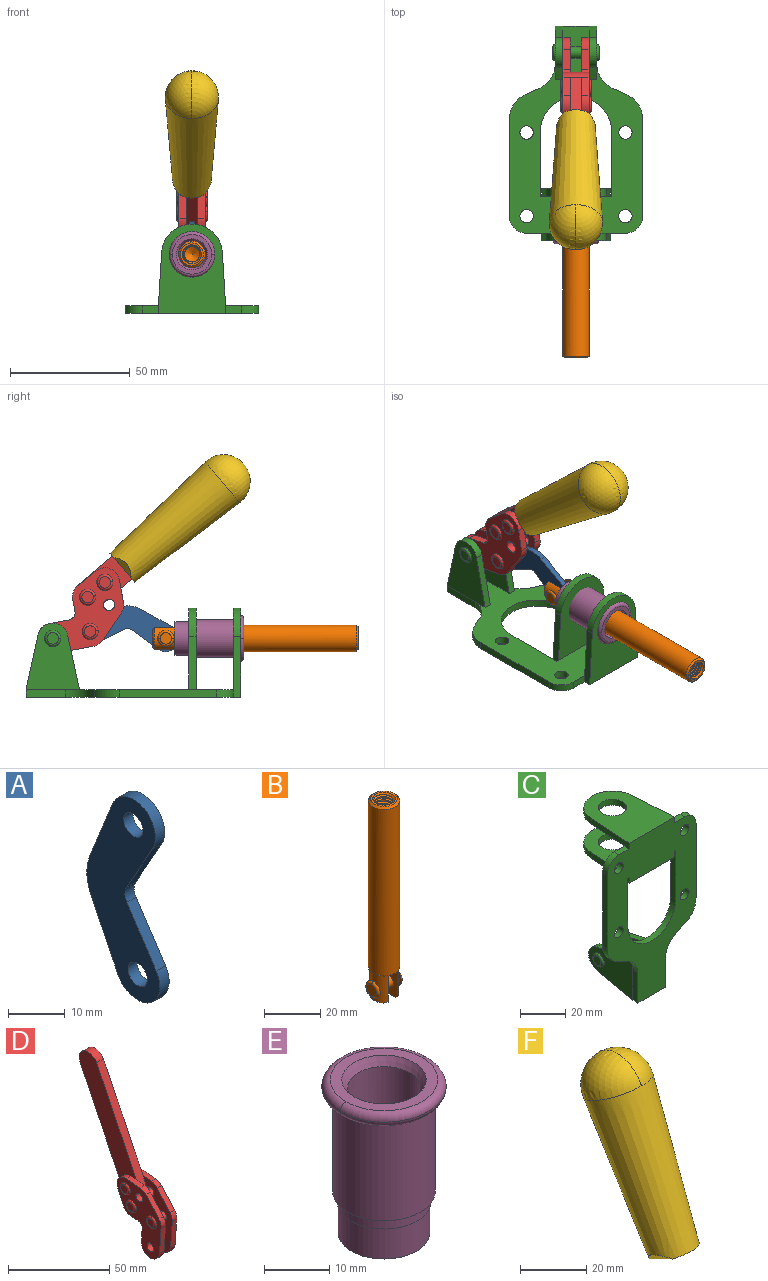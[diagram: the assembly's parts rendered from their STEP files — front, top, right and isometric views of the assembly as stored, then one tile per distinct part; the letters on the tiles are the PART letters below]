
ASSEMBLY  parts=6 mates=6
PART A: 12 faces, bbox 2.3x18.2x42.8 mm
  f0: cylinder r=2.4mm len=4.8mm, axis (1,0,0), area 34.9mm2, adj f4,f11
  f1: cylinder r=10.41mm len=8.47mm, axis (1,0,0), area 20.2mm2, adj f4,f9,f10,f11
  f2: cylinder r=3.05mm len=3.16mm, axis (1,0,0), area 7.7mm2, adj f4,f6,f7,f11
  f3: cylinder r=2.4mm len=4.8mm, axis (1,0,0), area 34.9mm2, adj f4,f11
  f4: plane 42.81x18.23mm, normal (-1,0,0), area 414.1mm2, adj f0,f1,f2,f3,f5,f6,f7,f8
  f5: cylinder r=5.54mm len=10.67mm, axis (1,0,0), area 41.8mm2, adj f4,f6,f10,f11
  f6: plane 11.66x6.53mm, normal (0,-0.87,-0.49), area 30.9mm2, adj f2,f4,f5,f11
  f7: plane 11.17x7.33mm, normal (0,-0.84,0.55), area 30.9mm2, adj f2,f4,f8,f11
  f8: cylinder r=5.54mm len=10.51mm, axis (1,0,0), area 41.8mm2, adj f4,f7,f9,f11
  f9: plane 13.67x6.67mm, normal (0,0.9,-0.44), area 35.1mm2, adj f1,f4,f8,f11
  f10: plane 14.1x5.7mm, normal (0,0.93,0.37), area 35.1mm2, adj f1,f4,f5,f11
  f11: plane 42.81x18.23mm, normal (1,0,0), area 414.1mm2, adj f0,f1,f2,f3,f5,f6,f7,f8
PART B: 48 faces, bbox 12.6x11.1x86.1 mm
  f0: torus R=2.41mm, axis (-1,0,0), area 15mm2, adj f30,f32,f34
  f1: torus R=2.41mm, axis (-1,0,0), area 15mm2, adj f29,f31,f33
  f2: cylinder r=5.54mm len=72.39mm, axis (0,0,1), area 2518.5mm2, adj f3,f4,f42,f43
  f3: cone r=5.54mm half-angle=45deg, axis (0,0,1), area 7.6mm2, adj f2,f5,f41
  f4: cone r=5.54mm half-angle=45deg, axis (0,0,-1), area 34.9mm2, adj f2,f39
  f5: cylinder r=5.08mm len=11.48mm, axis (0,0,1), area 108.3mm2, adj f3,f7,f8,f41
  f6: cylinder r=2.41mm len=4.83mm, axis (-1,0,0), area 71.2mm2, adj f40,f41
  f7: cylinder r=2.41mm len=4.83mm, axis (-1,0,0), area 7.6mm2, adj f5,f34
  f8: cone r=5.08mm half-angle=45deg, axis (0,0,1), area 10.6mm2, adj f5,f37,f41
  f9: cone r=3.98mm half-angle=45deg, axis (0,0,1), area 17.6mm2, adj f27,f39,f45,f46,f47
  f10: cylinder r=2.41mm len=4.83mm, axis (-1,0,0), area 7.6mm2, adj f33,f38
  f11: cylinder r=3.2mm len=6.4mm, axis (0,0,1), area 78.4mm2, adj f12,f28,f44,f45,f47
  f12: cylinder r=3.2mm len=6.4mm, axis (0,0,1), area 10.5mm2, adj f11,f13,f45,f47
  f13: cylinder r=3.2mm len=6.4mm, axis (0,0,1), area 10.5mm2, adj f12,f14,f45,f47
  f14: cylinder r=3.2mm len=6.4mm, axis (0,0,1), area 10.5mm2, adj f13,f15,f45,f47
  f15: cylinder r=3.2mm len=6.4mm, axis (0,0,1), area 10.5mm2, adj f14,f16,f45,f47
  f16: cylinder r=3.2mm len=6.4mm, axis (0,0,1), area 10.5mm2, adj f15,f17,f45,f47
  f17: cylinder r=3.2mm len=6.4mm, axis (0,0,1), area 10.5mm2, adj f16,f18,f45,f47
  f18: cylinder r=3.2mm len=6.4mm, axis (0,0,1), area 10.5mm2, adj f17,f19,f45,f47
  f19: cylinder r=3.2mm len=6.4mm, axis (0,0,1), area 10.5mm2, adj f18,f20,f45,f47
  f20: cylinder r=3.2mm len=6.4mm, axis (0,0,1), area 10.5mm2, adj f19,f21,f45,f47
  f21: cylinder r=3.2mm len=6.4mm, axis (0,0,1), area 10.5mm2, adj f20,f22,f45,f47
  f22: cylinder r=3.2mm len=6.4mm, axis (0,0,1), area 10.5mm2, adj f21,f23,f45,f47
  f23: cylinder r=3.2mm len=6.4mm, axis (0,0,1), area 10.5mm2, adj f22,f24,f45,f47
  f24: cylinder r=3.2mm len=6.4mm, axis (0,0,1), area 10.5mm2, adj f23,f25,f45,f47
  f25: cylinder r=3.2mm len=6.4mm, axis (0,0,1), area 10.5mm2, adj f24,f26,f45,f47
  f26: cylinder r=3.2mm len=6.4mm, axis (0,0,1), area 10.5mm2, adj f25,f27,f45,f47
  f27: cylinder r=3.2mm len=6.4mm, axis (0,0,1), area 7.4mm2, adj f9,f26,f45,f47
  f28: cone r=3.2mm half-angle=60deg, axis (0,0,1), area 37.2mm2, adj f11
  f29: plane 4.83x4.83mm, normal (-1,0,0), area 18.3mm2, adj f1,f31
  f30: plane 4.83x4.83mm, normal (1,0,0), area 18.3mm2, adj f0,f32
  f31: torus R=2.41mm, axis (-1,0,0), area 15mm2, adj f1,f29,f33
  f32: torus R=2.41mm, axis (-1,0,0), area 15mm2, adj f0,f30,f34
  f33: plane 6.83x6.83mm, normal (1,0,0), area 18.3mm2, adj f1,f10,f31
  f34: plane 6.83x6.83mm, normal (-1,0,0), area 18.3mm2, adj f0,f7,f32
  f35: cone r=5.08mm half-angle=45deg, axis (0,0,1), area 10.6mm2, adj f36,f38,f40
  f36: plane 7.25x1.97mm, normal (0,0,-1), area 10mm2, adj f35,f40
  f37: plane 7.25x1.97mm, normal (0,0,-1), area 10mm2, adj f8,f41
  f38: cylinder r=5.08mm len=11.48mm, axis (0,0,1), area 108.3mm2, adj f10,f35,f40,f42
  f39: plane 9.55x9.55mm, normal (0,0,1), area 22mm2, adj f4,f9
  f40: plane 12.76x10.09mm, normal (1,0,0), area 95.7mm2, adj f6,f35,f36,f38,f42,f43
  f41: plane 12.76x10.09mm, normal (-1,0,0), area 95.7mm2, adj f3,f5,f6,f8,f37,f43
  f42: cone r=5.54mm half-angle=45deg, axis (0,0,1), area 7.6mm2, adj f2,f38,f40
  f43: plane 11.07x4.7mm, normal (0,0,-1), area 50.4mm2, adj f2,f40,f41
  f44: plane 0.89x0.62mm, normal (-1,0,0), area 0.3mm2, adj f11,f45,f46,f47
  f45: bspline ~24.8x7.63mm, area 266.6mm2, adj f9,f11,f12,f13,f14,f15,f16,f17
  f46: bspline ~24.87x7.63mm, area 73.6mm2, adj f9,f44,f45,f47
  f47: bspline ~24.98x7.63mm, area 272.5mm2, adj f9,f11,f12,f13,f14,f15,f16,f17
PART C: 55 faces, bbox 55.7x37.4x89.8 mm
  f0: torus R=2.41mm, axis (-1,0,0), area 15mm2, adj f11,f15,f25
  f1: torus R=2.41mm, axis (-1,0,0), area 15mm2, adj f10,f12,f22
  f2: cylinder r=2.78mm len=5.56mm, axis (0,-1,0), area 54.2mm2, adj f30,f54
  f3: cylinder r=14.99mm len=29.97mm, axis (0,-1,0), area 145.9mm2, adj f30,f49,f53,f54
  f4: cylinder r=2.78mm len=5.56mm, axis (0,-1,0), area 54.2mm2, adj f30,f54
  f5: cylinder r=2.78mm len=5.56mm, axis (0,-1,0), area 54.2mm2, adj f30,f54
  f6: cylinder r=2.78mm len=5.56mm, axis (0,-1,0), area 54.2mm2, adj f30,f54
  f7: cylinder r=6.35mm len=12.7mm, axis (0,0,1), area 123.6mm2, adj f27,f51
  f8: cylinder r=6.35mm len=12.7mm, axis (0,0,-1), area 124.7mm2, adj f21,f35
  f9: cylinder r=2.41mm len=11.18mm, axis (-1,0,0), area 169.4mm2, adj f16,f19
  f10: plane 4.83x4.83mm, normal (1,0,0), area 18.3mm2, adj f1,f12
  f11: plane 4.83x4.83mm, normal (-1,0,0), area 18.3mm2, adj f0,f15
  f12: torus R=2.41mm, axis (-1,0,0), area 15mm2, adj f1,f10,f22
  f13: cylinder r=6.35mm len=12.41mm, axis (1,0,0), area 53.4mm2, adj f18,f19,f22,f23
  f14: cylinder r=6.35mm len=12.41mm, axis (-1,0,0), area 53.4mm2, adj f16,f17,f24,f25
  f15: torus R=2.41mm, axis (-1,0,0), area 15mm2, adj f0,f11,f25
  f16: plane 27.86x22.35mm, normal (1,0,0), area 425.4mm2, adj f9,f14,f17,f24,f30
  f17: plane 22.86x4.97mm, normal (0,0.21,0.98), area 72.5mm2, adj f14,f16,f25,f30
  f18: plane 22.86x4.97mm, normal (0,0.21,0.98), area 72.5mm2, adj f13,f19,f22,f30
  f19: plane 27.86x22.35mm, normal (-1,0,0), area 425.4mm2, adj f9,f13,f18,f23,f30
  f20: cylinder r=12.7mm len=25.35mm, axis (0,0,-1), area 119.8mm2, adj f21,f34,f35,f36
  f21: plane 34.21x28.07mm, normal (0,0,-1), area 702.4mm2, adj f8,f20,f30,f34,f36
  f22: plane 27.96x22.45mm, normal (1,0,0), area 407.2mm2, adj f1,f12,f13,f18,f23,f30,f42,f43
  f23: plane 22.86x4.97mm, normal (0,0.21,-0.98), area 72.5mm2, adj f13,f19,f22,f44
  f24: plane 22.86x4.97mm, normal (0,0.21,-0.98), area 72.5mm2, adj f14,f16,f25,f44
  f25: plane 27.86x22.35mm, normal (-1,0,0), area 407.1mm2, adj f0,f14,f15,f17,f24,f30,f45,f46
  f26: plane 3.1x0.95mm, normal (0,0,-1), area 2.7mm2, adj f30,f49,f50,f54
  f27: plane 34.21x28.07mm, normal (0,0,1), area 702.4mm2, adj f7,f28,f30,f50,f52
  f28: cylinder r=12.7mm len=25.35mm, axis (0,0,1), area 118.8mm2, adj f27,f50,f51,f52
  f29: plane 3.1x0.95mm, normal (0,0,-1), area 2.7mm2, adj f30,f52,f53,f54
  f30: plane 86.54x55.63mm, normal (0,1,0), area 2362.9mm2, adj f2,f3,f4,f5,f6,f16,f17,f18
  f31: plane 40.56x3.1mm, normal (-1,0,0), area 125.7mm2, adj f30,f32,f48,f54
  f32: cylinder r=7.11mm len=7.11mm, axis (0,-1,0), area 34.6mm2, adj f30,f31,f33,f54
  f33: plane 6.67x3.1mm, normal (0,0,1), area 20.4mm2, adj f30,f32,f34,f54
  f34: plane 25.39x3.13mm, normal (-1,0.06,0), area 79.5mm2, adj f20,f21,f33,f35,f54
  f35: plane 37.31x28.45mm, normal (0,0,1), area 789.9mm2, adj f8,f20,f34,f36,f54
  f36: plane 25.39x3.13mm, normal (1,0.06,0), area 79.5mm2, adj f20,f21,f35,f37,f54
  f37: plane 6.67x3.1mm, normal (0,0,1), area 20.4mm2, adj f30,f36,f38,f54
  f38: cylinder r=7.11mm len=7.11mm, axis (0,-1,0), area 34.6mm2, adj f30,f37,f39,f54
  f39: plane 40.56x3.1mm, normal (1,0,0), area 125.7mm2, adj f30,f38,f40,f54
  f40: cylinder r=11.18mm len=10.16mm, axis (0,-1,0), area 39.5mm2, adj f30,f39,f41,f54
  f41: plane 6.09x3.1mm, normal (0.42,0,-0.91), area 20.8mm2, adj f30,f40,f42,f54
  f42: cylinder r=11.18mm len=9.41mm, axis (0,-1,0), area 37.2mm2, adj f22,f30,f41,f43,f54
  f43: plane 16.5x3.1mm, normal (1,0,0), area 51.1mm2, adj f22,f42,f44,f54
  f44: plane 17.37x3.1mm, normal (0,0,-1), area 53.8mm2, adj f23,f24,f30,f43,f45,f54
  f45: plane 16.5x3.1mm, normal (-1,0,0), area 51.1mm2, adj f25,f44,f46,f54
  f46: cylinder r=11.18mm len=9.41mm, axis (0,-1,0), area 37.2mm2, adj f25,f30,f45,f47,f54
  f47: plane 6.09x3.1mm, normal (-0.42,0,-0.91), area 20.8mm2, adj f30,f46,f48,f54
  f48: cylinder r=11.18mm len=10.16mm, axis (0,-1,0), area 39.5mm2, adj f30,f31,f47,f54
  f49: plane 26.54x3.1mm, normal (-1,0,0), area 82.3mm2, adj f3,f26,f30,f54
  f50: plane 25.39x3.1mm, normal (1,0.06,0), area 78.8mm2, adj f26,f27,f28,f51,f54
  f51: plane 37.31x28.45mm, normal (0,0,-1), area 789.9mm2, adj f7,f28,f50,f52,f54
  f52: plane 25.39x3.1mm, normal (-1,0.06,0), area 78.8mm2, adj f27,f28,f29,f51,f54
  f53: plane 26.54x3.1mm, normal (1,0,0), area 82.3mm2, adj f3,f29,f30,f54
  f54: plane 89.66x55.63mm, normal (0,-1,0), area 2678.5mm2, adj f2,f3,f4,f5,f6,f26,f29,f31
PART D: 59 faces, bbox 12.9x60.2x99.6 mm
  f0: torus R=2.39mm, axis (-1,0,0), area 14.9mm2, adj f20,f43,f51
  f1: torus R=2.39mm, axis (-1,0,0), area 14.9mm2, adj f19,f42,f51
  f2: torus R=2.39mm, axis (-1,0,0), area 14.9mm2, adj f18,f35,f51
  f3: torus R=2.39mm, axis (-1,0,0), area 14.9mm2, adj f14,f17,f23
  f4: torus R=2.39mm, axis (-1,0,0), area 14.9mm2, adj f13,f16,f23
  f5: torus R=2.39mm, axis (-1,0,0), area 14.9mm2, adj f12,f15,f23
  f6: cylinder r=2.39mm len=4.78mm, axis (1,0,0), area 46.5mm2, adj f48,f50,f51
  f7: cylinder r=2.39mm len=4.78mm, axis (1,0,0), area 46.5mm2, adj f50,f51
  f8: cylinder r=6.35mm len=12.68mm, axis (1,0,0), area 61.8mm2, adj f38,f39,f50,f51
  f9: cylinder r=2.39mm len=4.78mm, axis (-1,0,0), area 70.5mm2, adj f46,f50
  f10: cylinder r=2.39mm len=4.78mm, axis (-1,0,0), area 46.5mm2, adj f23,f45,f46
  f11: cylinder r=2.39mm len=4.78mm, axis (-1,0,0), area 46.5mm2, adj f23,f46
  f12: plane 4.78x4.78mm, normal (1,0,0), area 17.9mm2, adj f5,f15
  f13: plane 4.78x4.78mm, normal (1,0,0), area 17.9mm2, adj f4,f16
  f14: plane 4.78x4.78mm, normal (1,0,0), area 17.9mm2, adj f3,f17
  f15: torus R=2.39mm, axis (-1,0,0), area 14.9mm2, adj f5,f12,f23
  f16: torus R=2.39mm, axis (-1,0,0), area 14.9mm2, adj f4,f13,f23
  f17: torus R=2.39mm, axis (-1,0,0), area 14.9mm2, adj f3,f14,f23
  f18: plane 4.78x4.78mm, normal (-1,0,0), area 17.9mm2, adj f2,f35
  f19: plane 4.78x4.78mm, normal (-1,0,0), area 17.9mm2, adj f1,f42
  f20: plane 4.78x4.78mm, normal (-1,0,0), area 17.9mm2, adj f0,f43
  f21: plane 2.26x0.2mm, normal (1,0,0), area 0.2mm2, adj f31,f44
  f22: plane 2.26x0.2mm, normal (-1,0,0), area 0.2mm2, adj f41,f44
  f23: plane 39.37x30.77mm, normal (1,0,0), area 565.5mm2, adj f3,f4,f5,f10,f11,f15,f16,f17
  f24: cylinder r=6.1mm len=4.15mm, axis (-1,0,0), area 14.7mm2, adj f23,f25,f32,f46
  f25: plane 10.25x9.01mm, normal (0,-0.75,0.66), area 42.3mm2, adj f23,f24,f26,f46
  f26: cylinder r=6.35mm len=4.64mm, axis (-1,0,0), area 15.6mm2, adj f23,f25,f27,f46
  f27: plane 15.84x3.1mm, normal (0,-1,-0.07), area 49.2mm2, adj f23,f26,f28,f46
  f28: cylinder r=6.35mm len=12.68mm, axis (-1,0,0), area 61.8mm2, adj f23,f27,f29,f46
  f29: plane 8.11x3.1mm, normal (0,1,0.07), area 25.2mm2, adj f23,f28,f30,f46
  f30: cylinder r=3.05mm len=3.25mm, axis (-1,0,0), area 14.8mm2, adj f23,f29,f31,f46
  f31: plane 5.99x3.1mm, normal (0,0.07,-1), area 18.6mm2, adj f21,f23,f30,f44,f46
  f32: plane 9.5x3.1mm, normal (0,-0.07,1), area 29.5mm2, adj f23,f24,f33,f46,f47
  f33: cylinder r=6.1mm len=8.63mm, axis (-1,0,0), area 39.1mm2, adj f23,f32,f34,f47
  f34: plane 8.65x3.96mm, normal (0,0.91,-0.42), area 29.5mm2, adj f23,f33,f44,f47
  f35: torus R=2.39mm, axis (-1,0,0), area 14.9mm2, adj f2,f18,f51
  f36: plane 10.25x9.01mm, normal (0,-0.75,0.66), area 42.3mm2, adj f37,f49,f50,f51
  f37: cylinder r=6.35mm len=4.64mm, axis (1,0,0), area 15.6mm2, adj f36,f38,f50,f51
  f38: plane 15.84x3.1mm, normal (0,-1,-0.07), area 49.2mm2, adj f8,f37,f50,f51
  f39: plane 8.11x3.1mm, normal (0,1,0.07), area 25.2mm2, adj f8,f40,f50,f51
  f40: cylinder r=3.05mm len=3.25mm, axis (1,0,0), area 14.8mm2, adj f39,f41,f50,f51
  f41: plane 5.99x3.1mm, normal (0,0.07,-1), area 18.6mm2, adj f22,f40,f44,f50,f51
  f42: torus R=2.39mm, axis (-1,0,0), area 14.9mm2, adj f1,f19,f51
  f43: torus R=2.39mm, axis (-1,0,0), area 14.9mm2, adj f0,f20,f51
  f44: cylinder r=6.35mm len=12.12mm, axis (-1,0,0), area 128.9mm2, adj f21,f22,f23,f31,f34,f41,f46,f47
  f45: plane 2.65x1.35mm, normal (1,0,0), area 1mm2, adj f10,f55
  f46: plane 39.08x20.42mm, normal (-1,0,0), area 412.5mm2, adj f9,f10,f11,f24,f25,f26,f27,f28
  f47: plane 77.62x39.82mm, normal (1,0,0), area 850mm2, adj f32,f33,f34,f44,f53,f54,f55
  f48: plane 2.65x1.35mm, normal (-1,0,0), area 1mm2, adj f6,f55
  f49: cylinder r=6.1mm len=4.15mm, axis (1,0,0), area 14.7mm2, adj f36,f50,f51,f56
  f50: plane 39.08x20.42mm, normal (1,0,0), area 412.5mm2, adj f6,f7,f8,f9,f36,f37,f38,f39
  f51: plane 39.37x30.77mm, normal (-1,0,0), area 565.5mm2, adj f0,f1,f2,f6,f7,f8,f35,f36
  f52: plane 8.65x3.96mm, normal (0,0.91,-0.42), area 29.5mm2, adj f44,f51,f57,f58
  f53: plane 68.49x33.4mm, normal (0,0.9,-0.44), area 358.1mm2, adj f44,f47,f54,f58
  f54: cylinder r=6.35mm len=12.06mm, axis (1,0,0), area 93.7mm2, adj f47,f53,f55,f58
  f55: plane 68.49x33.4mm, normal (0,-0.9,0.44), area 358.1mm2, adj f44,f45,f46,f47,f48,f50,f54,f58
  f56: plane 9.5x3.1mm, normal (0,-0.07,1), area 29.5mm2, adj f49,f50,f51,f57,f58
  f57: cylinder r=6.1mm len=8.63mm, axis (1,0,0), area 39.1mm2, adj f51,f52,f56,f58
  f58: plane 77.62x39.82mm, normal (-1,0,0), area 850mm2, adj f44,f52,f53,f54,f55,f56,f57
PART E: 15 faces, bbox 20.6x20.6x28.7 mm
  f0: torus R=8.26mm, axis (0,0,1), area 56.8mm2, adj f1,f10,f12
  f1: torus R=8.26mm, axis (0,0,1), area 56.8mm2, adj f0,f6,f13
  f2: cylinder r=5.59mm len=25.91mm, axis (0,0,1), area 909.6mm2, adj f3,f4
  f3: cone r=6.86mm half-angle=45deg, axis (0,0,-1), area 70.2mm2, adj f2,f14
  f4: cone r=6.47mm half-angle=30deg, axis (0,0,1), area 66.7mm2, adj f2,f13
  f5: cylinder r=7.04mm len=14.07mm, axis (0,0,1), area 252.6mm2, adj f11,f14
  f6: torus R=8.26mm, axis (0,0,1), area 56.8mm2, adj f1,f12,f13
  f7: cylinder r=7.16mm len=14.33mm, axis (0,0,1), area 91.5mm2, adj f9,f11
  f8: cylinder r=7.86mm len=18.42mm, axis (0,0,1), area 909.6mm2, adj f9,f10
  f9: plane 15.72x15.72mm, normal (0,0,-1), area 33mm2, adj f7,f8
  f10: plane 16.51x16.51mm, normal (0,0,-1), area 19.9mm2, adj f0,f8,f12
  f11: plane 14.33x14.33mm, normal (0,0,-1), area 5.7mm2, adj f5,f7
  f12: torus R=8.26mm, axis (0,0,1), area 56.8mm2, adj f0,f6,f10
  f13: plane 16.51x16.51mm, normal (0,0,1), area 82.7mm2, adj f1,f4,f6
  f14: plane 14.07x14.07mm, normal (0,0,-1), area 7.8mm2, adj f3,f5
PART F: 11 faces, bbox 22.3x42.6x64.5 mm
  f0: sphere r=11.13mm, area 411.4mm2, adj f1,f8
  f1: cone r=11.11mm half-angle=3.3deg, axis (0,0.44,0.9), area 3251.8mm2, adj f0,f7,f8,f9,f10
  f2: cylinder r=6.16mm len=11.7mm, axis (1,0,0), area 89.5mm2, adj f3,f4,f5,f6
  f3: plane 60.23x36.75mm, normal (-1,0,0), area 763.6mm2, adj f2,f4,f6,f10
  f4: plane 51.37x25.05mm, normal (0,0.9,-0.44), area 264.2mm2, adj f2,f3,f5,f10
  f5: plane 60.23x36.75mm, normal (1,0,0), area 763.6mm2, adj f2,f4,f6,f10
  f6: plane 51.37x25.05mm, normal (0,-0.9,0.44), area 264.2mm2, adj f2,f3,f5,f10
  f7: plane 9.95x5.95mm, normal (0.71,-0.31,-0.64), area 25.8mm2, adj f1,f10
  f8: sphere r=11.13mm, area 411.4mm2, adj f0,f1
  f9: plane 9.95x5.95mm, normal (-0.71,-0.31,-0.64), area 25.8mm2, adj f1,f10
  f10: plane 14.27x11.38mm, normal (0,-0.44,-0.9), area 106.7mm2, adj f1,f3,f4,f5,f6,f7,f9
PLACE A rot(axis=(0,-0.69,-0.73),180deg) t=(0,11.54,2.05)mm
PLACE B rot(axis=(1,0,0),90deg) t=(0,9.48,0)mm
PLACE C rot(axis=(1,0,0),90deg) t=(0,9.14,0)mm fixed
PLACE D rot(axis=(1,0,0),75.6deg) t=(0,4.02,8.78)mm
PLACE E rot(axis=(1,0,0),90deg) t=(0,10.41,0)mm
PLACE F rot(axis=(1,0,0),75.6deg) t=(-0.04,4.02,8.78)mm
MATE revolute D.f7 <-> C.f0  axis (-1,0,0) through (0,41.23,24.61)mm
MATE revolute A.f5 <-> D.f4  axis (-1,0,0) through (0,25.62,27.49)mm
MATE fastened F.f2 <-> D.f54  axis (1,0,0) through (-2.35,-31.31,91.23)mm
MATE slider B.f2 <-> E.f2  axis (0,-1,0) through (0,-49.31,24.61)mm
MATE revolute A.f3 <-> B.f6  axis (-1,0,0) through (0,-6,24.61)mm
MATE fastened E.f2 <-> C.f7  axis (0,-1,0) through (0,-37.25,24.61)mm
